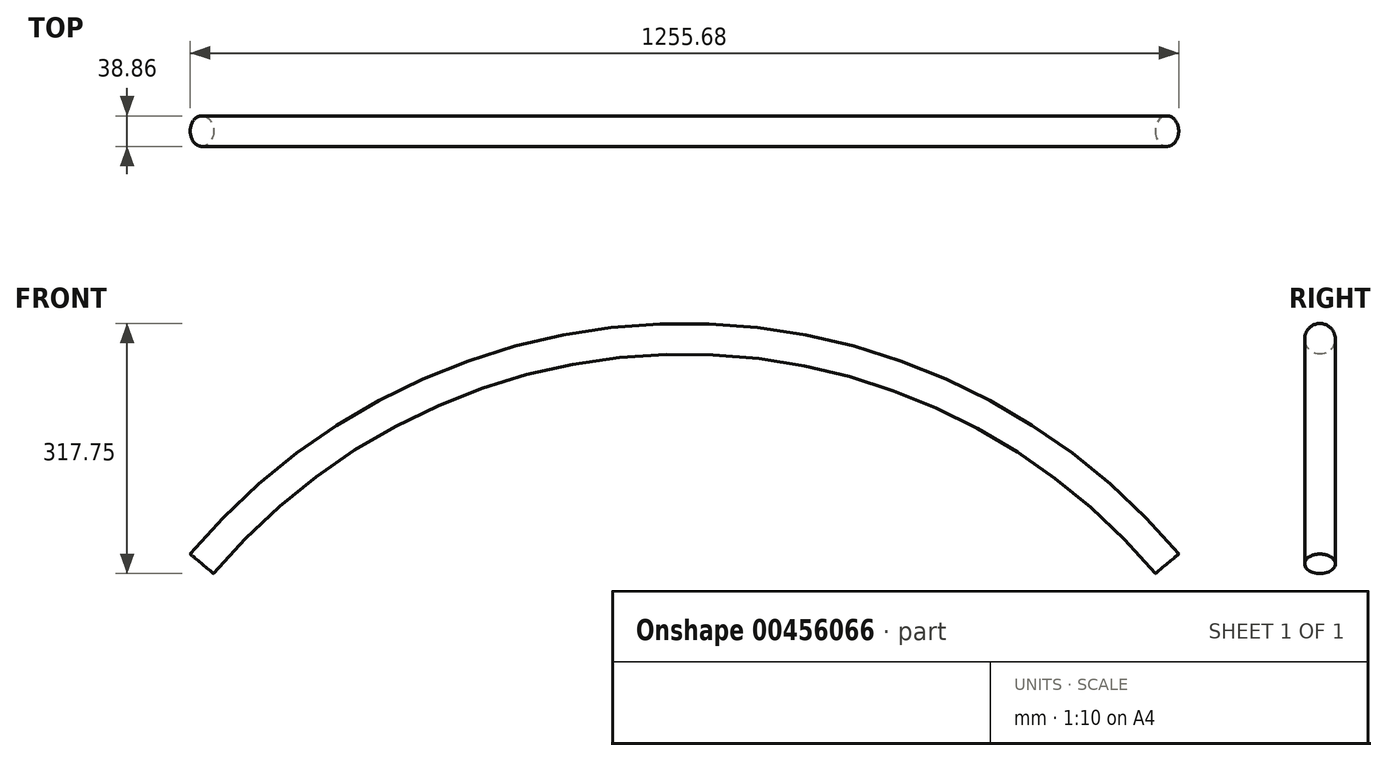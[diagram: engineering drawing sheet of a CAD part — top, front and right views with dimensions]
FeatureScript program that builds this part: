
annotation { "Feature Type Name" : "Feature", "Feature Type Description" : "" }
export const myFeature = defineFeature(function(context is Context, id is Id, definition is map)
    precondition{}
    {
        {
            var Q0;
            Q0=qCreatedBy(makeId("Top.planeOp"),FACE);
            var sketch = newSketch(context, id + "F0", { "sketchPlane" : qUnion([Q0])});
            skLineSegment(sketch, "E0", {"start": v(0, 0) * mm, "end": v(800.15, 0) * mm});
            skCircle(sketch, "E1", {"center": v(800.15, 0) * mm, "radius": 19.43 * mm});
            skLineSegment(sketch, "E2", {"start": v(0, 18.17) * mm, "end": v(0, -26.19) * mm});
            skSolve(sketch);
        }
        {
            var Q0;
            Q0=makeQuery(id+"F0.imprint","IMPRINT",FACE,{"disambiguationData":[TD([[makeQuery(id+"F0.imprint","IMPRINT",EDGE,{"derivedFrom":sQuery(id+"F0.wireOp",EDGE,"E1")}),1.0]])]});
            var Q1;
            Q1=sQuery(id+"F0.wireOp",EDGE,"E2");
            revolve(context, id + "F1", {"entities" : qUnion([Q0]), "axis" : qUnion([Q1]), "revolveType" : RevolveType.TWO_DIRECTIONS, "oppositeDirection" : true, "angle" : 320 * degree, "angleBack" : 220 * degree});
        }
    });
